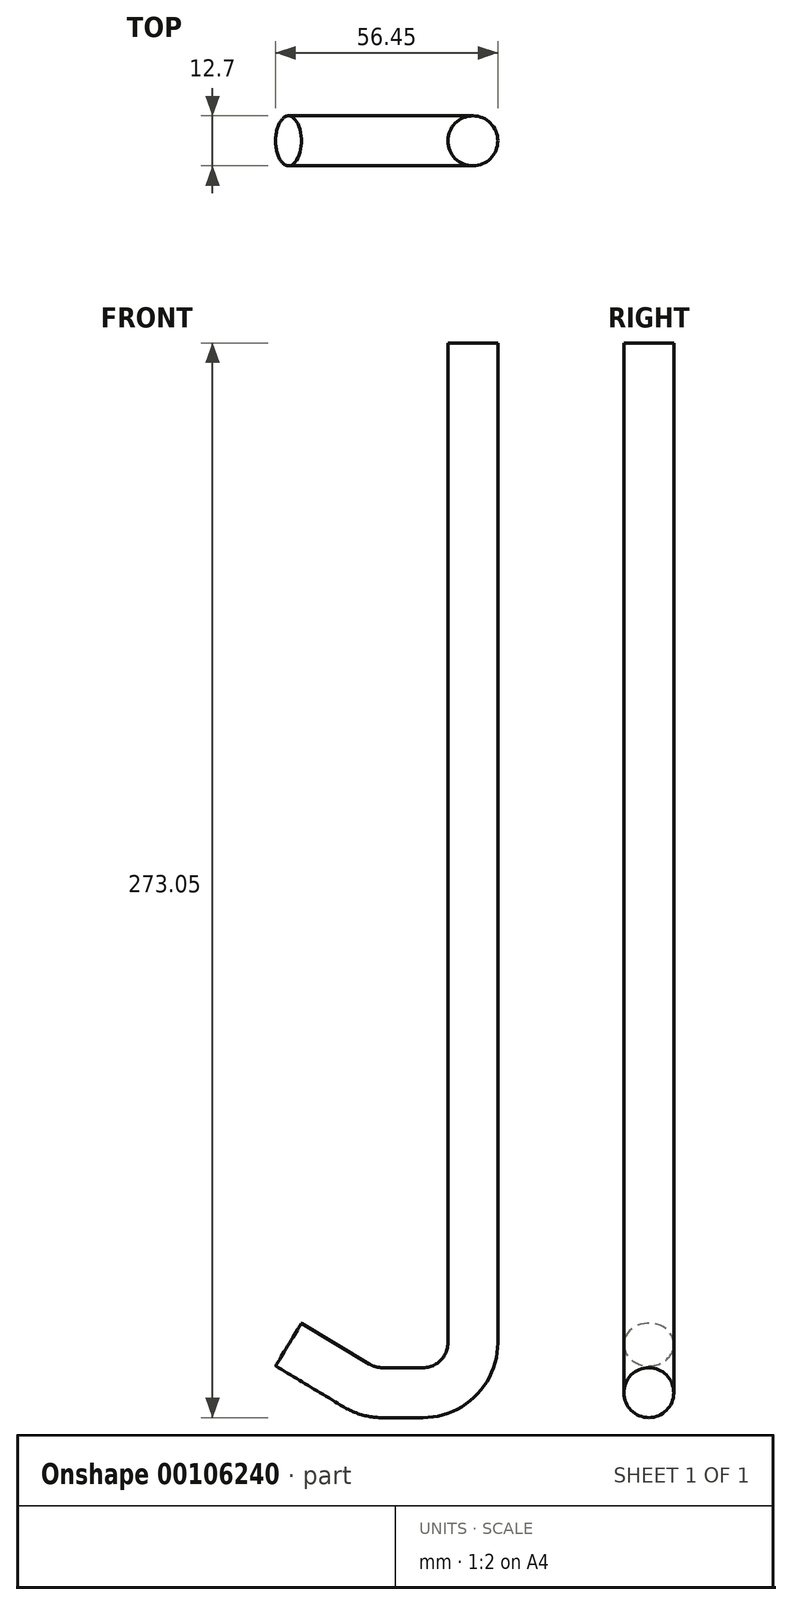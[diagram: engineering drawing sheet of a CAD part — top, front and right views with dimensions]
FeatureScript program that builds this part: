
annotation { "Feature Type Name" : "Feature", "Feature Type Description" : "" }
export const myFeature = defineFeature(function(context is Context, id is Id, definition is map)
    precondition{}
    {
        {
            var Q0;
            Q0=qCreatedBy(makeId("Front.planeOp"),FACE);
            var sketch = newSketch(context, id + "F0", { "sketchPlane" : qUnion([Q0])});
            skLineSegment(sketch, "E0", {"start": v(0, 202.63) * mm, "end": v(0, -51.37) * mm});
            skLineSegment(sketch, "E1", {"start": v(-12.7, -64.07) * mm, "end": v(-23, -64.07) * mm});
            skLineSegment(sketch, "E2", {"start": v(-29.55, -62.25) * mm, "end": v(-46.83, -51.85) * mm});
            skPoint(sketch, "E3.visualSharp", {"position": v(0, -64.07) * mm});
            skArc(sketch, "E3.filletArc", {"start": v(-12.7, -64.07) * mm, "mid": v(-3.72, -60.35) * mm, "end": v(0, -51.37) * mm});
            skPoint(sketch, "E4.visualSharp", {"position": v(-26.52, -64.07) * mm});
            skArc(sketch, "E4.filletArc", {"start": v(-29.55, -62.25) * mm, "mid": v(-26.4, -63.6) * mm, "end": v(-23, -64.07) * mm});
            skSolve(sketch);
        }
        {
            var Q0;
            Q0=sQuery(id+"F0.wireOp",VERTEX,"E0.start");
            var Q1;
            Q1=qCreatedBy(makeId("Top.planeOp"),FACE);
            cPlane(context, id + "F1", {"entities" : qUnion([Q0, Q1]), "cplaneType" : CPlaneType.PLANE_POINT, "offset" : 25.4 * mm, "width" : 152.4 * mm, "height" : 152.4 * mm});
        }
        {
            var Q0;
            Q0=qCreatedBy(id+"F1.planeOp",FACE);
            var sketch = newSketch(context, id + "F2", { "sketchPlane" : qUnion([Q0])});
            skCircle(sketch, "E5", {"center": v(0, 0) * mm, "radius": 6.35 * mm});
            skSolve(sketch);
        }
        {
            var Q0;
            Q0=makeQuery(id+"F2.imprint","IMPRINT",FACE,{"disambiguationData":[TD([[makeQuery(id+"F2.imprint","IMPRINT",EDGE,{"derivedFrom":sQuery(id+"F2.wireOp",EDGE,"E5")}),1.0]])]});
            var Q1;
            Q1=sQuery(id+"F0.wireOp",EDGE,"E0");
            var Q2;
            Q2=sQuery(id+"F0.wireOp",EDGE,"E3.filletArc");
            var Q3;
            Q3=sQuery(id+"F0.wireOp",EDGE,"E1");
            var Q4;
            Q4=sQuery(id+"F0.wireOp",EDGE,"E4.filletArc");
            var Q5;
            Q5=sQuery(id+"F0.wireOp",EDGE,"E2");
            sweep(context, id + "F3", {"profiles" : qUnion([Q0]), "path" : qUnion([Q1, Q2, Q3, Q4, Q5])});
        }
    });
